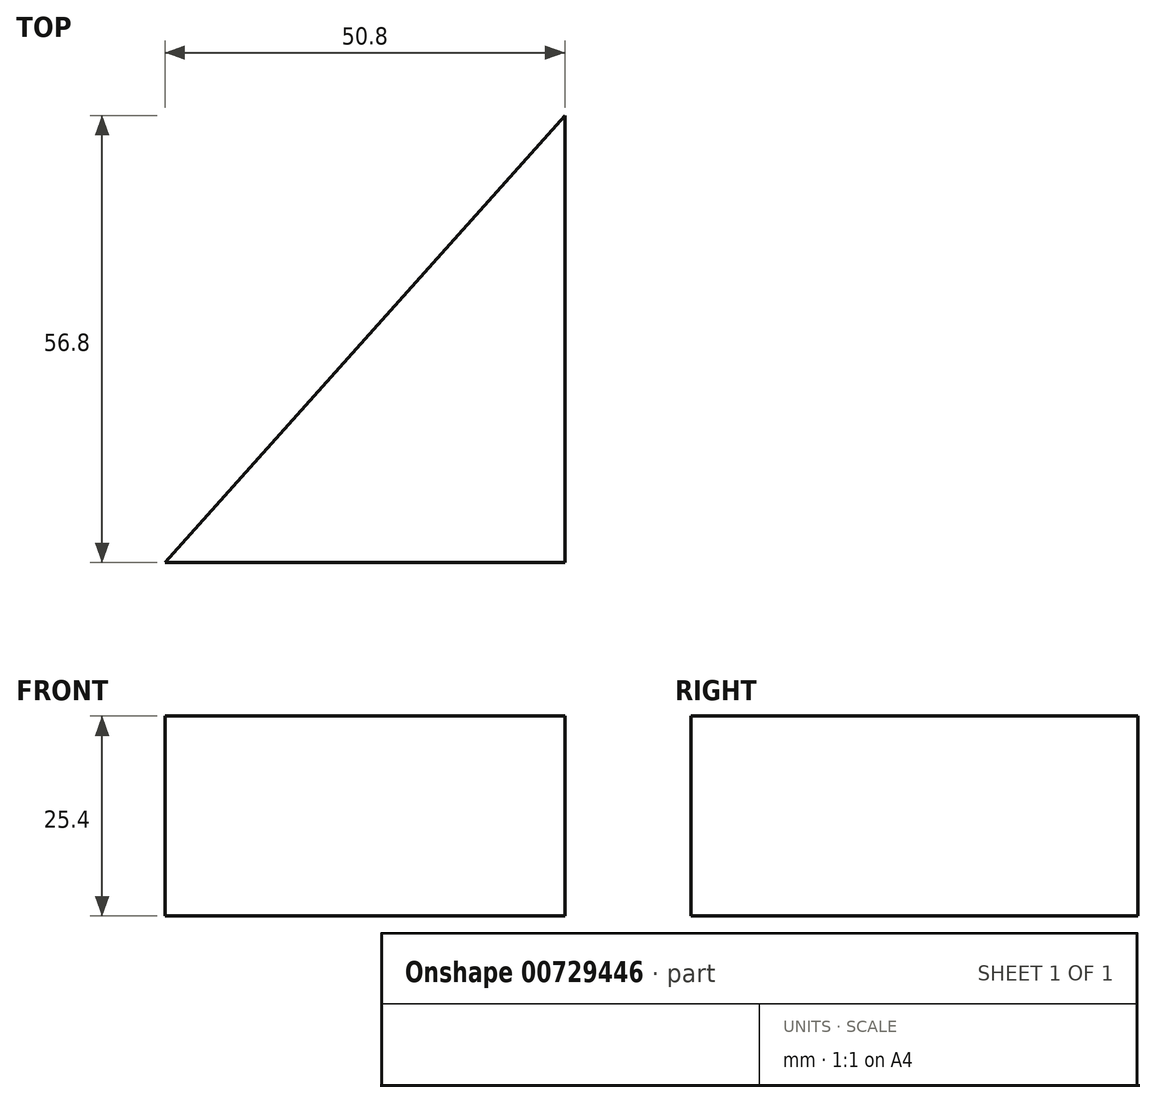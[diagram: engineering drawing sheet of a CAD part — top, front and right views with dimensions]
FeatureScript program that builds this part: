
annotation { "Feature Type Name" : "Feature", "Feature Type Description" : "" }
export const myFeature = defineFeature(function(context is Context, id is Id, definition is map)
    precondition{}
    {
        {
            var Q0;
            Q0=qCreatedBy(makeId("Top.planeOp"),FACE);
            var sketch = newSketch(context, id + "F0", { "sketchPlane" : qUnion([Q0])});
            skLineSegment(sketch, "E0", {"start": v(0, 0) * mm, "end": v(50.8, 56.8) * mm});
            skLineSegment(sketch, "E1", {"start": v(50.8, 0) * mm, "end": v(0, 0) * mm});
            skLineSegment(sketch, "E2", {"start": v(50.8, 56.8) * mm, "end": v(50.8, 0) * mm});
            skSolve(sketch);
        }
        {
            var Q0;
            Q0=makeQuery(id+"F0.imprint","IMPRINT",FACE,{"disambiguationData":[TD([[makeQuery(id+"F0.imprint","IMPRINT",EDGE,{"derivedFrom":sQuery(id+"F0.wireOp",EDGE,"E0")}),-1.0]])]});
            extrude(context, id + "F1", {"entities" : qUnion([Q0]), "depth" : 25.4 * mm, "offsetDistance" : 25.4 * mm});
        }
    });
